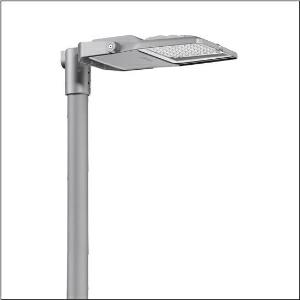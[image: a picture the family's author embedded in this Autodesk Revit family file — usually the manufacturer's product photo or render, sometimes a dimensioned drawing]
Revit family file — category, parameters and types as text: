
# Revit family: floodlight_fl_21_mini___pl52_5xa7775c2d3a_b3eb
name_source: partatom
category: Lighting Fixtures
units: mm (PartAtom-declared; Revit-internal decimal feet)

## family parameters
Cut with Voids When Loaded = No
Host = Face
Light Source = No
Part Type = Normal
Room Calculation Point = No
Round Connector Dimension = Use Diameter
Shared = No

## types (1)
- --- (1 x LED, 12190 lm, 89 W, 3000K)
    Apparent Load = 89 VA
    CIE Flux Codes = 26 60 98 100 100
    Color Rendering = 70
    Color Temperature = 3000K
    Default Elevation = 1800 mm
    Description = Floodlight FL 21 mini, floodlight, primary light control with lens, of PMMA, primary optical cover: protective disc, of toughened safety glass, transparent, light distribution: PL52, light emission: direct distribution, installation type: surface-mounted, LED, High Power LED, rated luminous flux: 12.190lm, luminous efficacy: 137lm/W, light colour: 730, colour temperature: 3000K, control: flexible luminous flux parameterisation, time-dependent luminous flux control, constant luminous flux control, overheat protection, pre-setting: logarithmic dimming characteristic, with terminal, 6-pole, mains connection: 220..240V, AC, 50/60Hz, start of lifetime: 89W, end of service life: 94W, reduction: 43W, luminaire housing, of diecast aluminium, powder-coated, Siteco® metallic grey (DB 702S), corrosivity category C5 mid according to DIN EN ISO 12944, sealing non-destructively replaceable, please order mast flange separately, mast bracket, of steel, galvanised, powder-coated, Siteco® metallic grey (DB 702S), Smart Interface above, protection rating (complete): IP66, insulation class (complete): insulation class II (safety insulation), certification: CE, ENEC, VDE, protection symbol: D, impact resistance: IK08, permissible operating ambient temperature: -40..+40°C, permissible operating ambient temperature for outdoor applications: -40..+50°C, standard: DIN EN 12944, LABS conformity tested according to VDMA 24364:2018-05, packaging unit: 1 piece

Light Distribution: PL52
    Height = 70 mm
    Lamp = 1 x LED
    Lamp Light Flux = 12190 lm
    Lamp Power = 89 W
    Lamp count = 1
    Length = 485 mm
    Luminous efficacy = 137 lm/W
    Manufacturer = Siteco
    ModVariant = No
    Model = 5XA7775C2D3A
    Number of Poles = 1
    OnlyDefault = Yes
    Power Factor = 1
    Product Name = Floodlight FL 21 mini | PL52
    Product group = floodlight | pylon annexe
    ProductGroupID = 6200
    Protection Class = Protection class II
    Protection Degree = IP 66
    RLX_Detail_Level = 1
    RLX_Emergency_Light_Flux = 0 lm
    RLX_Emergency_Type = 0
    RLX_Emergency_Type_DB = No
    RlxData = <blob elided: 100961 chars, md5=06e4666a>
    Socket = socket
    Standby Power = 0 W
    System Light Flux = 12190 lm
    System Power = 89 W
    Type Comments = factory setting: luminous flux: 100 % | dim-lin: 254 | 456 mA
    Type Image = l_1007125.jpg
    URL = http://relux.com
    VarID = @adj_133655
    Voltage = 0 V
    Weight = 0.00 kg
    Width = 337 mm

## geometry (parser evidence)
native form markers: Blend x4, Sweep x12
no freeform markers — native parametric forms only
